# Revit family: 3f_filippi_-_3f_linux_l_medio_3f_filippi_-_a20754_-_3f_linux_l_85_led_medio_l1778__ip54__e726
name_source: partatom
category: Lighting Fixtures
units: mm (PartAtom-declared; Revit-internal decimal feet)

## family parameters
Cut with Voids When Loaded = No
Host = Face
Light Source = No
Part Type = Normal
Room Calculation Point = No
Round Connector Dimension = Use Diameter
Shared = No

## types (1)
- 3F Filippi - 3F Linux L Medio (1 x LED, 13200 lm, 84 W, 4000 K)
    Apparent Load = 84 VA
    Approval mark = CE
    CIE Flux Codes = 69 90 97 96 100
    Color Rendering = 80
    Color Temperature = 4000 K
    Control Gear = Electronic ballast
    Default Elevation = 1800 mm
    Description = Light unit for structure continues 3F Linux S.

ILLUMINOTECHNICAL
Luminous efficiency 100% (DLOR 96%, ULOR 4%).
Initial luminous flux of the luminaire 13200 lm.
Direct symmetric medium distribution.
Installation Interdistance Transv.D = 1.17 x hu - Long.D = 1.18 x hu.
Tabular UGR (CIE 117 - 4H-8H; S=0.25H; 70/50/20): RUG 23 - 22.3.
Beam angle: 74° - 74°.
Luminous efficacy 157 lm/W.
Lifetime (L93/B10): 30000 h. (tq+25°C)
Lifetime (L90/B10): 50000 h. (tq+25°C)
Lifetime (L85/B10): 80000 h. (tq+25°C)
Lifetime (L80/B10): 100000 h. (tq+25°C)
Sudden decreased luminous flux after 50000 hours: 0% (C0).
Photobiological safety in compliance with IEC/TR 62778: RG0 risk exempt, (IEC 62471).
In compliance with IEC/EN 62722-2-1 - IEC/EN 62717 standards.

SOURCE
Linear LED module 85W/840.
Energy efficiency class (UE 2019/2020 - UE 2019/2015): C.
CIE 13.3 Colour rendering index: CRI >80 (R9 <50%).
IES TM-30 Fidelity Index: Rf = 84 Rg = 95.
CCT nominal colour temperature 4000 K.
Colour initial tolerance (MacAdam): SDCM 3.

MECHANICAL
Light unit in hot-galvanised steel, painted in white polyester base with fixing springs and retractable safety hooks in stainless steel.
Lenses for medium distribution, in transparent methacrylate (PMMA) with external flat surface.
Luminaire with limited surface temperature. - D - (EN 60598-2-24)
Dimensions: 1778x65 mm, height 71 mm. Weight 2.18 kg.
IP40 protection degree.
In combination with the appropriate accessories: IP54 protection degree.
Mechanical strength to impacts IK06 (1 joule).
Glow-wire test resistance 650°C.

ELECTRICAL
Halogen Free electronic wiring 230V-50/60Hz, power factor 0.95, THD <25%, constant output current, class I, 1 driver.
Power of the luminaire 84 W.
CE - IEC 60598-1 - EN 60598-1.
SAFE FLICKER: PstLM=<1 and SVM=<0.4 (IEC TR 61547-1 and IEC TR 63158), to ensure a more comfortable and safe light.
Luminaire compliant with EN 60598-2-22 for power supply from a centralised emergency system CPSS (Central Power Supply System), not incorporated in the luminaire - high risk areas excluded. The default power and flux are 100% in AC and 100% in DC.
Ambient temperature from 0°C to +25°C.
Temperature class T6 max 85°C.
Connection to the structure with 3-pin plug with phase selection (H05Z-U Halogen Free cable section 0.5 mm² HT90).
Relative humidity UR: <85%.

INSTALLATION
Ceiling / Suspended / Wall.
All accessories dedicated to this product are available on the Catalog and on our website www.3F-Filippi.com.

STRUCTURE
Hot-galvanised wired structure, painted in polyester base white, obtained through rolling process, with expanded EPDM rubber profiles.
Linear connecting element in hot galvanised steel with gasket for the formation of continuous channels, standard on L3556 versions (optional for other lengths).
Transparent polycarbonate IP54 cover element with methacrylate (PMMA) flexible parts.
The L3556 versions have a locking collar for joining the covers.
A20723 - 33F Linux system 7P IP54 L3556, structure with through-wiring 7-pole.
A20724 - 33F Linux system 7P IP54 L1778, structure with through-wiring 7-pole.
A20725 - 33F Linux system 5P IP54 L3556, structure with through-wiring 5-pole.
A20726 - 33F Linux system 5P IP54 L1778, structure with through-wiring 5-pole.

APPLICATIONS
Suitable product for food production plants (HACCP), IFS (Food Version 6), BRC (GSFS Food Version 7).
In commercial environments, exhibition areas, shops and stores.

WARNING
Luminaire designed for disposal/recycling at end-of-life.
Replaceable (LED only) light source by a professional. Replaceable control gear by a professional.
    Height = 71 mm
    Lamp = 1 x LED
    Lamp Light Flux = 13200 lm
    Lamp Power = 84 W
    Lamp count = 1
    Length = 1778 mm
    Lifetime = 50000 h
    Luminous efficacy = 157 lm/W
    Manufacturer = 3F Filippi
    ModVariant = No
    Model = 3F Filippi - A20754 - 3F Linux L 85 LED MEDIO L1778 (IP54)
    Mounting Place = Ceiling
    Mounting Type = Pendant
    Number of Poles = 1
    OnlyDefault = Yes
    Power Factor = 1
    Product Name = 3F Filippi - 3F Linux L Medio
    Product group = pendant luminaire
    ProductGroupID = 9
    Protection Class = Protection class I
    Protection Degree = IP 54
    RLX_Detail_Level = 1
    RLX_Emergency_Light_Flux = 0 lm
    RLX_Emergency_Type = 0
    RLX_Emergency_Type_DB = No
    RlxData = <blob elided: 46373 chars, md5=7e6cde27>
    Socket = socket
    Standby Power = 0 W
    System Light Flux = 13200 lm
    System Power = 84 W
    Type Comments = Product without accessories
    Type Image = 3ffilippi_3f_linux_l_ip54.jpg
    URL = http://relux.com
    VarID = ---
    Voltage = 0 V
    Weight = 0.00 kg
    Width = 65 mm

## geometry (parser evidence)
native form markers: Sweep x11
no freeform markers — native parametric forms only
